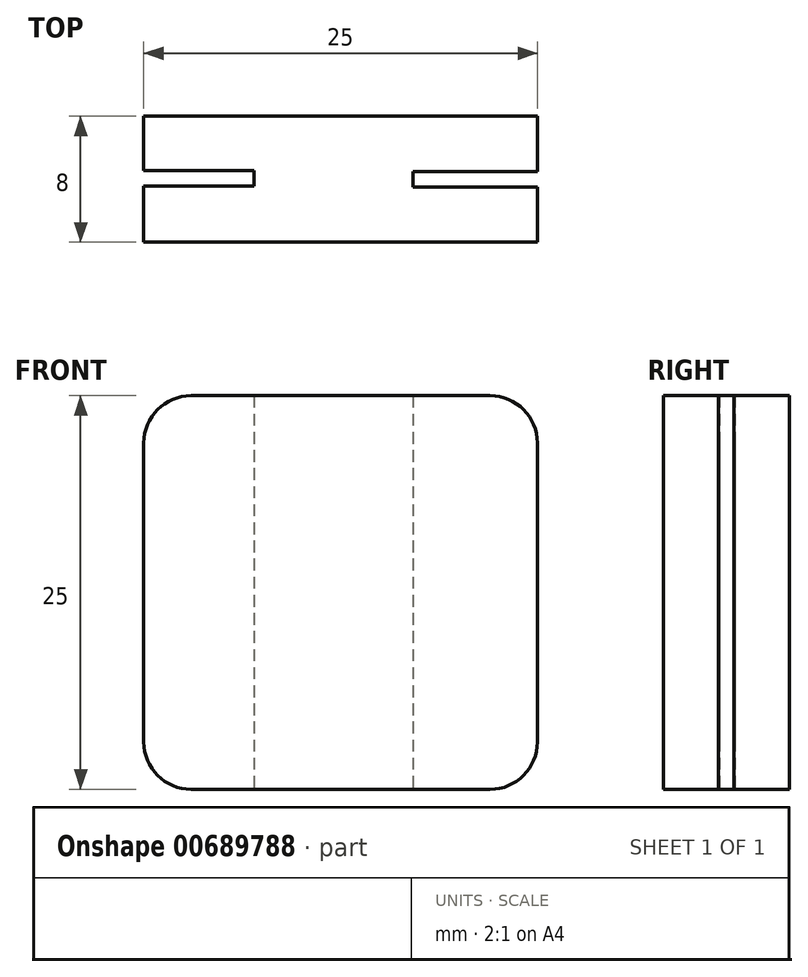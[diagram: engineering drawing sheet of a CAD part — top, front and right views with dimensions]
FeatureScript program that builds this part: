
annotation { "Feature Type Name" : "Feature", "Feature Type Description" : "" }
export const myFeature = defineFeature(function(context is Context, id is Id, definition is map)
    precondition{}
    {
        {
            var Q0;
            Q0=qCreatedBy(makeId("Front.planeOp"),FACE);
            var sketch = newSketch(context, id + "F0", { "sketchPlane" : qUnion([Q0])});
            skLineSegment(sketch, "E0.bottom", {"start": v(-12.97, 12.78) * mm, "end": v(12.03, 12.78) * mm});
            skLineSegment(sketch, "E0.top", {"start": v(-12.97, -12.22) * mm, "end": v(12.03, -12.22) * mm});
            skLineSegment(sketch, "E0.left", {"start": v(-12.97, 12.78) * mm, "end": v(-12.97, -12.22) * mm});
            skLineSegment(sketch, "E0.right", {"start": v(12.03, 12.78) * mm, "end": v(12.03, -12.22) * mm});
            skSolve(sketch);
        }
        {
            var Q0;
            Q0 = qSketchRegion(id + "F0", true);
            extrude(context, id + "F1", {"entities" : qUnion([Q0]), "depth" : 8 * mm, "offsetDistance" : 25 * mm});
        }
        {
            var Q0;
            Q0=makeQuery(id+"F1.opExtrude","SWEPT_FACE",FACE,{"disambiguationData":[OSD([sQuery(id+"F0.wireOp",EDGE,"E0.left")])]});
            var sketch = newSketch(context, id + "F2", { "sketchPlane" : qUnion([Q0])});
            skLineSegment(sketch, "E1.bottom", {"start": v(3.45, 12.78) * mm, "end": v(4.45, 12.78) * mm});
            skLineSegment(sketch, "E1.top", {"start": v(3.45, -12.22) * mm, "end": v(4.45, -12.22) * mm});
            skLineSegment(sketch, "E1.left", {"start": v(3.45, 12.78) * mm, "end": v(3.45, -12.22) * mm});
            skLineSegment(sketch, "E1.right", {"start": v(4.45, 12.78) * mm, "end": v(4.45, -12.22) * mm});
            skSolve(sketch);
        }
        {
            var Q0;
            Q0=makeQuery(id+"F2.imprint","IMPRINT",FACE,{"disambiguationData":[TD([[makeQuery(id+"F2.imprint","IMPRINT",EDGE,{"derivedFrom":sQuery(id+"F2.wireOp",EDGE,"E1.bottom")}),1.0]])]});
            extrude(context, id + "F3", {"entities" : qUnion([Q0]), "operationType" : NewBodyOperationType.REMOVE, "oppositeDirection" : true, "depth" : 7 * mm, "offsetDistance" : 25 * mm});
        }
        {
            var Q0;
            Q0=makeQuery(id+"F1.opExtrude","SWEPT_FACE",FACE,{"disambiguationData":[OSD([sQuery(id+"F0.wireOp",EDGE,"E0.right")])]});
            var sketch = newSketch(context, id + "F4", { "sketchPlane" : qUnion([Q0])});
            skLineSegment(sketch, "E2.bottom", {"start": v(-4.5, 12.78) * mm, "end": v(-3.5, 12.78) * mm});
            skLineSegment(sketch, "E2.top", {"start": v(-4.5, -12.22) * mm, "end": v(-3.5, -12.22) * mm});
            skLineSegment(sketch, "E2.left", {"start": v(-4.5, 12.78) * mm, "end": v(-4.5, -12.22) * mm});
            skLineSegment(sketch, "E2.right", {"start": v(-3.5, 12.78) * mm, "end": v(-3.5, -12.22) * mm});
            skSolve(sketch);
        }
        {
            var Q0;
            Q0=makeQuery(id+"F4.imprint","IMPRINT",FACE,{"disambiguationData":[TD([[makeQuery(id+"F4.imprint","IMPRINT",EDGE,{"derivedFrom":sQuery(id+"F4.wireOp",EDGE,"E2.bottom")}),-1.0]])]});
            extrude(context, id + "F5", {"entities" : qUnion([Q0]), "operationType" : NewBodyOperationType.REMOVE, "oppositeDirection" : true, "depth" : 7.9 * mm, "offsetDistance" : 25 * mm});
        }
        {
            var Q0;
            {var subQ0=sQuery(id+"F0.wireOp",EDGE,"E0.bottom");var subQ1=sQuery(id+"F0.wireOp",EDGE,"E0.left");Q0=makeQuery(id+"F3.boolean.opBoolean","SPLIT",EDGE,{"disambiguationData":[TD([makeQuery(id+"F3.opExtrude","SWEPT_FACE",FACE,{"disambiguationData":[OSD([sQuery(id+"F2.wireOp",EDGE,"E1.left")])]})])],"derivedFrom":makeQuery(id+"F1.opExtrude","SWEPT_EDGE",EDGE,{"disambiguationData":[OSD([subQ0,subQ1])]})});}
            var Q1;
            {var subQ0=sQuery(id+"F0.wireOp",EDGE,"E0.bottom");var subQ1=sQuery(id+"F0.wireOp",EDGE,"E0.left");Q1=makeQuery(id+"F3.boolean.opBoolean","SPLIT",EDGE,{"disambiguationData":[TD([makeQuery(id+"F3.opExtrude","SWEPT_FACE",FACE,{"disambiguationData":[OSD([sQuery(id+"F2.wireOp",EDGE,"E1.right")])]})])],"derivedFrom":makeQuery(id+"F1.opExtrude","SWEPT_EDGE",EDGE,{"disambiguationData":[OSD([subQ0,subQ1])]})});}
            var Q2;
            {var subQ0=sQuery(id+"F0.wireOp",EDGE,"E0.bottom");var subQ1=sQuery(id+"F0.wireOp",EDGE,"E0.right");Q2=makeQuery(id+"F5.boolean.opBoolean","SPLIT",EDGE,{"disambiguationData":[TD([makeQuery(id+"F5.opExtrude","SWEPT_FACE",FACE,{"disambiguationData":[OSD([sQuery(id+"F4.wireOp",EDGE,"E2.left")])]})])],"derivedFrom":makeQuery(id+"F1.opExtrude","SWEPT_EDGE",EDGE,{"disambiguationData":[OSD([subQ0,subQ1])]})});}
            var Q3;
            {var subQ0=sQuery(id+"F0.wireOp",EDGE,"E0.bottom");var subQ1=sQuery(id+"F0.wireOp",EDGE,"E0.right");Q3=makeQuery(id+"F5.boolean.opBoolean","SPLIT",EDGE,{"disambiguationData":[TD([makeQuery(id+"F5.opExtrude","SWEPT_FACE",FACE,{"disambiguationData":[OSD([sQuery(id+"F4.wireOp",EDGE,"E2.right")])]})])],"derivedFrom":makeQuery(id+"F1.opExtrude","SWEPT_EDGE",EDGE,{"disambiguationData":[OSD([subQ0,subQ1])]})});}
            var Q4;
            {var subQ0=sQuery(id+"F0.wireOp",EDGE,"E0.right");var subQ1=sQuery(id+"F0.wireOp",EDGE,"E0.top");Q4=makeQuery(id+"F5.boolean.opBoolean","SPLIT",EDGE,{"disambiguationData":[TD([makeQuery(id+"F5.opExtrude","SWEPT_FACE",FACE,{"disambiguationData":[OSD([sQuery(id+"F4.wireOp",EDGE,"E2.right")])]})])],"derivedFrom":makeQuery(id+"F1.opExtrude","SWEPT_EDGE",EDGE,{"disambiguationData":[OSD([subQ1,subQ0])]})});}
            var Q5;
            {var subQ0=sQuery(id+"F0.wireOp",EDGE,"E0.right");var subQ1=sQuery(id+"F0.wireOp",EDGE,"E0.top");Q5=makeQuery(id+"F5.boolean.opBoolean","SPLIT",EDGE,{"disambiguationData":[TD([makeQuery(id+"F5.opExtrude","SWEPT_FACE",FACE,{"disambiguationData":[OSD([sQuery(id+"F4.wireOp",EDGE,"E2.left")])]})])],"derivedFrom":makeQuery(id+"F1.opExtrude","SWEPT_EDGE",EDGE,{"disambiguationData":[OSD([subQ1,subQ0])]})});}
            var Q6;
            {var subQ0=sQuery(id+"F0.wireOp",EDGE,"E0.left");var subQ1=sQuery(id+"F0.wireOp",EDGE,"E0.top");Q6=makeQuery(id+"F3.boolean.opBoolean","SPLIT",EDGE,{"disambiguationData":[TD([makeQuery(id+"F3.opExtrude","SWEPT_FACE",FACE,{"disambiguationData":[OSD([sQuery(id+"F2.wireOp",EDGE,"E1.left")])]})])],"derivedFrom":makeQuery(id+"F1.opExtrude","SWEPT_EDGE",EDGE,{"disambiguationData":[OSD([subQ1,subQ0])]})});}
            var Q7;
            {var subQ0=sQuery(id+"F0.wireOp",EDGE,"E0.left");var subQ1=sQuery(id+"F0.wireOp",EDGE,"E0.top");Q7=makeQuery(id+"F3.boolean.opBoolean","SPLIT",EDGE,{"disambiguationData":[TD([makeQuery(id+"F3.opExtrude","SWEPT_FACE",FACE,{"disambiguationData":[OSD([sQuery(id+"F2.wireOp",EDGE,"E1.right")])]})])],"derivedFrom":makeQuery(id+"F1.opExtrude","SWEPT_EDGE",EDGE,{"disambiguationData":[OSD([subQ1,subQ0])]})});}
            fillet(context, id + "F6", {"entities" : qUnion([Q0, Q1, Q2, Q3, Q4, Q5, Q6, Q7]), "radius" : 3 * mm, "tangentPropagation" : true, "allowEdgeOverflow" : false});
        }
    });
